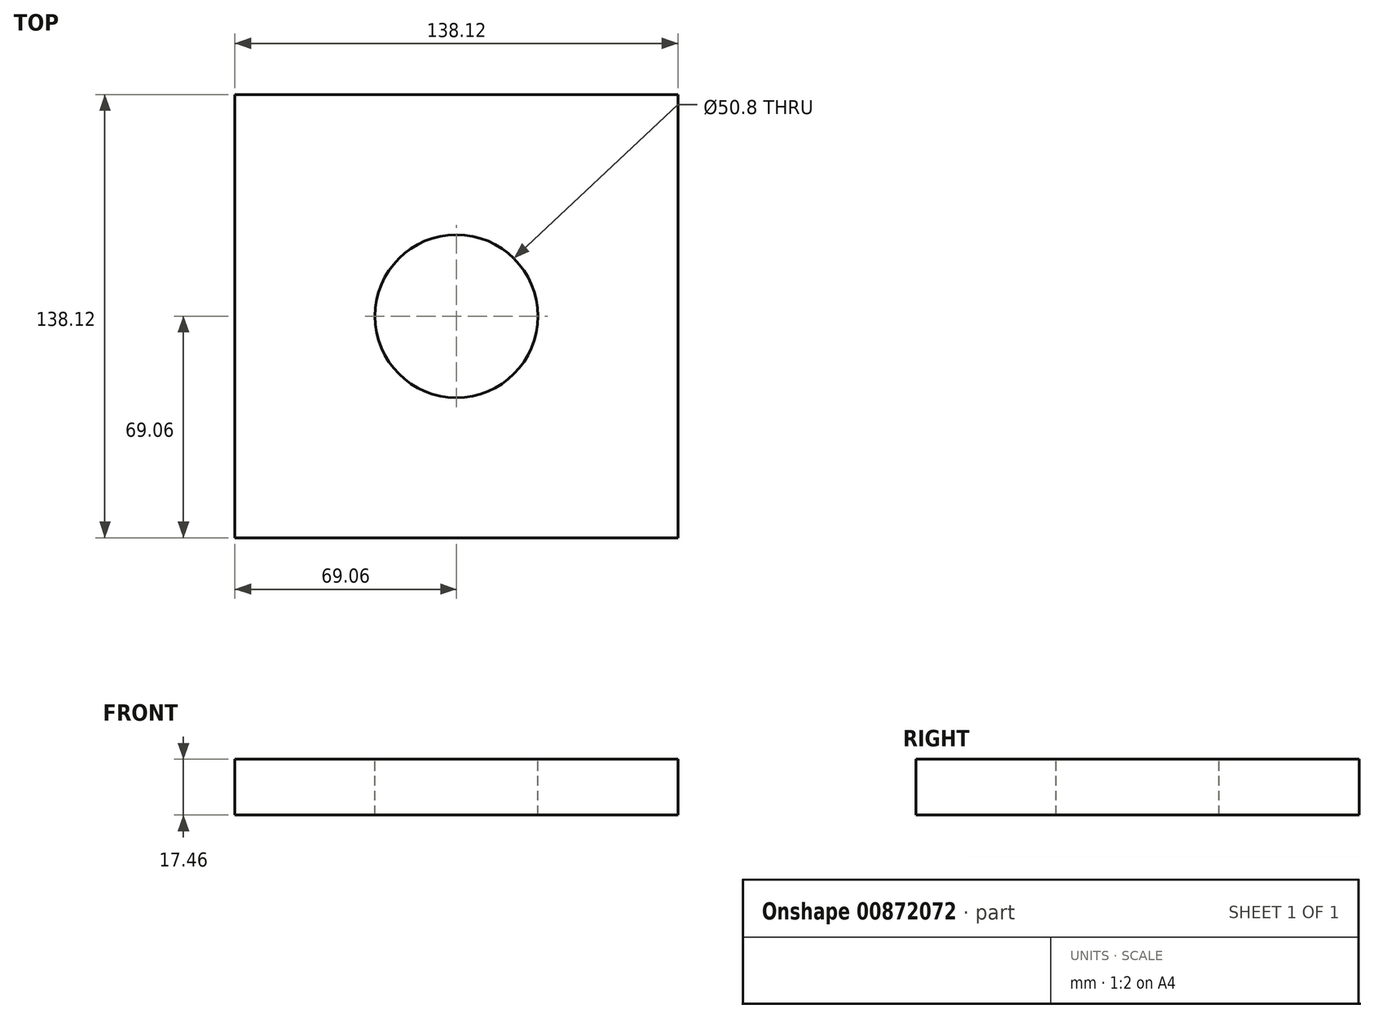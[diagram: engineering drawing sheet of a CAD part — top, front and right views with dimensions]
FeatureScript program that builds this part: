
annotation { "Feature Type Name" : "Feature", "Feature Type Description" : "" }
export const myFeature = defineFeature(function(context is Context, id is Id, definition is map)
    precondition{}
    {
        {
            var Q0;
            Q0=qCreatedBy(makeId("Top.planeOp"),FACE);
            var sketch = newSketch(context, id + "F0", { "sketchPlane" : qUnion([Q0])});
            skLineSegment(sketch, "E0.bottom", {"start": v(69.06, 69.06) * mm, "end": v(-69.06, 69.06) * mm});
            skLineSegment(sketch, "E0.top", {"start": v(69.06, -69.06) * mm, "end": v(-69.06, -69.06) * mm});
            skLineSegment(sketch, "E0.left", {"start": v(69.06, 69.06) * mm, "end": v(69.06, -69.06) * mm});
            skLineSegment(sketch, "E0.right", {"start": v(-69.06, 69.06) * mm, "end": v(-69.06, -69.06) * mm});
            skPoint(sketch, "E0.middle", {"position": v(0, 0) * mm});
            skSolve(sketch);
        }
        {
            var Q0;
            Q0=qSketchRegion(id+"F0",true);
            extrude(context, id + "F1", {"entities" : qUnion([Q0]), "depth" : 17.46 * mm});
        }
        {
            var Q0;
            Q0=makeQuery(id+"F1.opExtrude","CAP_FACE",FACE,{"disambiguationData":[OSD([sQuery(id+"F0.wireOp",EDGE,"E0.bottom"),sQuery(id+"F0.wireOp",EDGE,"E0.top"),sQuery(id+"F0.wireOp",EDGE,"E0.left"),sQuery(id+"F0.wireOp",EDGE,"E0.right")])],"isStart":false});
            var sketch = newSketch(context, id + "F2", { "sketchPlane" : qUnion([Q0])});
            skCircle(sketch, "E1", {"center": v(0, 0) * mm, "radius": 25.4 * mm});
            skSolve(sketch);
        }
        {
            var Q0;
            Q0=qSketchRegion(id+"F2",true);
            extrude(context, id + "F3", {"entities" : qUnion([Q0]), "operationType" : NewBodyOperationType.REMOVE, "oppositeDirection" : true, "depth" : 25.4 * mm});
        }
    });
